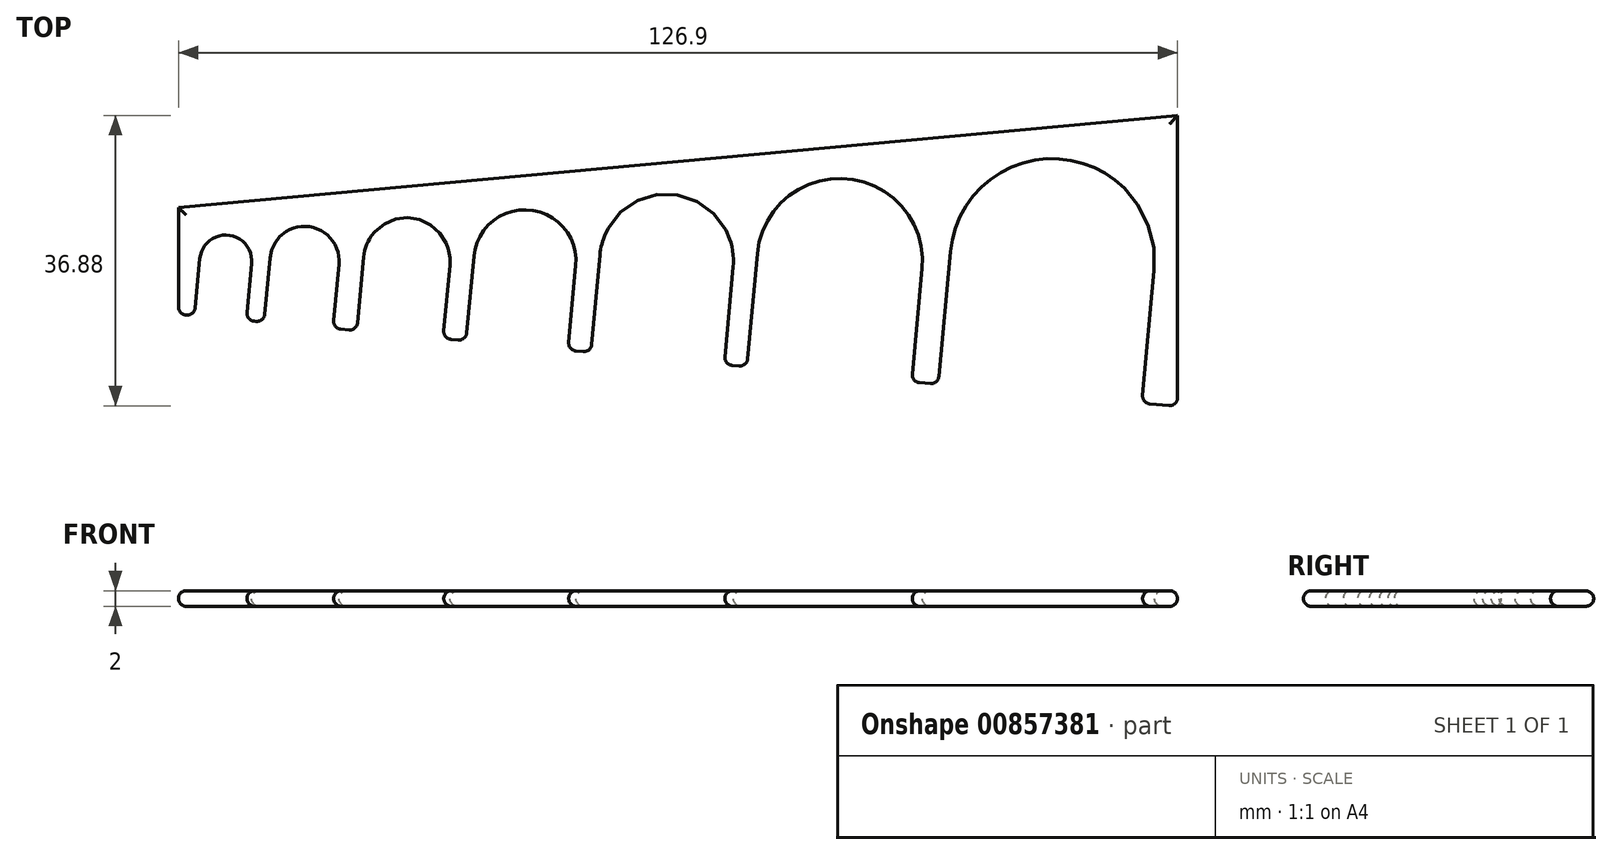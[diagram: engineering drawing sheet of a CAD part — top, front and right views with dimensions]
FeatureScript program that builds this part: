
annotation { "Feature Type Name" : "Feature", "Feature Type Description" : "" }
export const myFeature = defineFeature(function(context is Context, id is Id, definition is map)
    precondition{}
    {
        {
            var Q0;
            Q0=qCreatedBy(makeId("Top.planeOp"),FACE);
            var sketch = newSketch(context, id + "F0", { "sketchPlane" : qUnion([Q0])});
            skCircle(sketch, "E0", {"center": v(0, 0) * mm, "radius": 4.4 * mm});
            skCircle(sketch, "E1", {"center": v(-10, 0) * mm, "radius": 3.3 * mm});
            skCircle(sketch, "E2", {"center": v(13, 0) * mm, "radius": 5.5 * mm});
            skCircle(sketch, "E3", {"center": v(28, 0) * mm, "radius": 6.5 * mm});
            skArc(sketch, "E4", {"start": v(54.46, -0.78) * mm, "mid": v(46.78, 8.46) * mm, "end": v(37.54, 0.78) * mm});
            skArc(sketch, "E5", {"start": v(66.14, -10.33) * mm, "mid": v(67.03, -10.46) * mm, "end": v(67.94, -10.5) * mm});
            skCircle(sketch, "E6", {"center": v(95, 0) * mm, "radius": 13 * mm});
            skLineSegment(sketch, "E7", {"start": v(-16, -6.76) * mm, "end": v(-16, 0) * mm});
            skLineSegment(sketch, "E8", {"start": v(110.9, 0) * mm, "end": v(110.9, -18.49) * mm});
            skLineSegment(sketch, "E9", {"start": v(-10, -3.3) * mm, "end": v(95, -13) * mm});
            skLineSegment(sketch, "E10.0", {"start": v(-16, -6.76) * mm, "end": v(110.9, -18.49) * mm});
            skLineSegment(sketch, "E11", {"start": v(-16, 0) * mm, "end": v(110.9, 0) * mm});
            skLineSegment(sketch, "E12.MirrorCS", {"start": v(-16, 6.76) * mm, "end": v(110.9, 18.49) * mm});
            skLineSegment(sketch, "E13", {"start": v(-16, 0) * mm, "end": v(-16, 6.76) * mm});
            skLineSegment(sketch, "E14", {"start": v(110.9, 0) * mm, "end": v(110.9, 18.49) * mm});
            skLineSegment(sketch, "E15", {"start": v(-10, 0) * mm, "end": v(-10.67, -7.26) * mm});
            skLineSegment(sketch, "E16", {"start": v(0, 0) * mm, "end": v(-0.75, -8.17) * mm});
            skLineSegment(sketch, "E17", {"start": v(13, 0) * mm, "end": v(12.14, -9.36) * mm});
            skLineSegment(sketch, "E18", {"start": v(28, 0) * mm, "end": v(27, -10.74) * mm});
            skLineSegment(sketch, "E19", {"start": v(68, 0) * mm, "end": v(66.67, -14.4) * mm});
            skLineSegment(sketch, "E20", {"start": v(95, 0) * mm, "end": v(93.44, -16.87) * mm});
            skLineSegment(sketch, "E21", {"start": v(80.5, -15.68) * mm, "end": v(82.06, 1.2) * mm});
            skLineSegment(sketch, "E22", {"start": v(106.39, -18.07) * mm, "end": v(107.94, -1.2) * mm});
            skLineSegment(sketch, "E23", {"start": v(77.13, -15.37) * mm, "end": v(78.46, -0.97) * mm});
            skLineSegment(sketch, "E24", {"start": v(56.21, -13.43) * mm, "end": v(57.54, 0.97) * mm});
            skArc(sketch, "E25.trimOffspring", {"start": v(78.46, -0.97) * mm, "mid": v(68.97, 10.46) * mm, "end": v(57.54, 0.97) * mm});
            skLineSegment(sketch, "E26", {"start": v(54.46, -0.78) * mm, "end": v(53.32, -13.17) * mm});
            skLineSegment(sketch, "E27", {"start": v(37.54, 0.78) * mm, "end": v(36.4, -11.6) * mm});
            skLineSegment(sketch, "E28", {"start": v(28, 0) * mm, "end": v(34.47, -0.6) * mm});
            skLineSegment(sketch, "E29", {"start": v(34.47, -0.6) * mm, "end": v(33.48, -11.33) * mm});
            skLineSegment(sketch, "E30", {"start": v(28, 0) * mm, "end": v(21.53, 0.6) * mm});
            skLineSegment(sketch, "E31", {"start": v(21.53, 0.6) * mm, "end": v(20.54, -10.14) * mm});
            skLineSegment(sketch, "E32", {"start": v(13, 0) * mm, "end": v(18.48, -0.5) * mm});
            skLineSegment(sketch, "E33", {"start": v(18.48, -0.5) * mm, "end": v(17.61, -9.87) * mm});
            skLineSegment(sketch, "E34", {"start": v(13, 0) * mm, "end": v(7.52, 0.5) * mm});
            skLineSegment(sketch, "E35", {"start": v(7.52, 0.5) * mm, "end": v(6.66, -8.86) * mm});
            skLineSegment(sketch, "E36", {"start": v(0, 0) * mm, "end": v(4.38, -0.4) * mm});
            skLineSegment(sketch, "E37", {"start": v(4.38, -0.4) * mm, "end": v(3.63, -8.58) * mm});
            skLineSegment(sketch, "E38", {"start": v(0, 0) * mm, "end": v(-4.38, 0.4) * mm});
            skLineSegment(sketch, "E39", {"start": v(-4.38, 0.4) * mm, "end": v(-5.14, -7.77) * mm});
            skLineSegment(sketch, "E40", {"start": v(-10, 0) * mm, "end": v(-6.71, -0.3) * mm});
            skLineSegment(sketch, "E41", {"start": v(-6.71, -0.3) * mm, "end": v(-7.38, -7.56) * mm});
            skLineSegment(sketch, "E42", {"start": v(-10, 0) * mm, "end": v(-13.29, 0.3) * mm});
            skLineSegment(sketch, "E43", {"start": v(-13.29, 0.3) * mm, "end": v(-13.96, -6.95) * mm});
            skSolve(sketch);
        }
        {
            var Q0;
            Q0=makeQuery(id+"F0.imprint","IMPRINT",FACE,{"disambiguationData":[TD([[makeQuery(id+"F0.imprint","IMPRINT",EDGE,{"derivedFrom":sQuery(id+"F0.wireOp",EDGE,"E12.MirrorCS")}),-1.0]])]});
            var Q1;
            {var subQ0=sQuery(id+"F0.wireOp",EDGE,"E7");Q1=makeQuery(id+"F0.imprint","IMPRINT",FACE,{"disambiguationData":[TD([[makeQuery(id+"F0.imprint","IMPRINT",EDGE,{"derivedFrom":subQ0}),-1.0]])]});}
            var Q2;
            {var subQ1=sQuery(id+"F0.wireOp",EDGE,"E9");var subQ7=sQuery(id+"F0.wireOp",EDGE,"E41");var subQ8=makeQuery(id+"F0.imprint","INTERSECT",VERTEX,{"derivedFrom":[subQ1,subQ7]});Q2=makeQuery(id+"F0.imprint","IMPRINT",FACE,{"disambiguationData":[TD([[makeQuery(id+"F0.imprint","IMPRINT",EDGE,{"disambiguationData":[TD([[subQ8,-1.0]])],"derivedFrom":subQ1}),1.0]])]});}
            var Q3;
            {var subQ0=sQuery(id+"F0.wireOp",EDGE,"E41");var subQ1=sQuery(id+"F0.wireOp",EDGE,"E9");var subQ2=makeQuery(id+"F0.imprint","INTERSECT",VERTEX,{"derivedFrom":[subQ1,subQ0]});Q3=makeQuery(id+"F0.imprint","IMPRINT",FACE,{"disambiguationData":[TD([[makeQuery(id+"F0.imprint","IMPRINT",EDGE,{"disambiguationData":[TD([[subQ2,-1.0]])],"derivedFrom":subQ1}),-1.0]])]});}
            var Q4;
            {var subQ1=sQuery(id+"F0.wireOp",EDGE,"E9");var subQ7=sQuery(id+"F0.wireOp",EDGE,"E37");var subQ8=makeQuery(id+"F0.imprint","INTERSECT",VERTEX,{"derivedFrom":[subQ1,subQ7]});Q4=makeQuery(id+"F0.imprint","IMPRINT",FACE,{"disambiguationData":[TD([[makeQuery(id+"F0.imprint","IMPRINT",EDGE,{"disambiguationData":[TD([[subQ8,-1.0]])],"derivedFrom":subQ1}),1.0]])]});}
            var Q5;
            {var subQ0=sQuery(id+"F0.wireOp",EDGE,"E37");var subQ1=sQuery(id+"F0.wireOp",EDGE,"E9");var subQ2=makeQuery(id+"F0.imprint","INTERSECT",VERTEX,{"derivedFrom":[subQ1,subQ0]});Q5=makeQuery(id+"F0.imprint","IMPRINT",FACE,{"disambiguationData":[TD([[makeQuery(id+"F0.imprint","IMPRINT",EDGE,{"disambiguationData":[TD([[subQ2,-1.0]])],"derivedFrom":subQ1}),-1.0]])]});}
            var Q6;
            {var subQ1=sQuery(id+"F0.wireOp",EDGE,"E9");var subQ7=sQuery(id+"F0.wireOp",EDGE,"E33");var subQ9=makeQuery(id+"F0.imprint","INTERSECT",VERTEX,{"derivedFrom":[subQ1,subQ7]});Q6=makeQuery(id+"F0.imprint","IMPRINT",FACE,{"disambiguationData":[TD([[makeQuery(id+"F0.imprint","IMPRINT",EDGE,{"disambiguationData":[TD([[subQ9,-1.0]])],"derivedFrom":subQ1}),1.0]])]});}
            var Q7;
            {var subQ0=sQuery(id+"F0.wireOp",EDGE,"E33");var subQ1=sQuery(id+"F0.wireOp",EDGE,"E9");var subQ2=makeQuery(id+"F0.imprint","INTERSECT",VERTEX,{"derivedFrom":[subQ1,subQ0]});Q7=makeQuery(id+"F0.imprint","IMPRINT",FACE,{"disambiguationData":[TD([[makeQuery(id+"F0.imprint","IMPRINT",EDGE,{"disambiguationData":[TD([[subQ2,-1.0]])],"derivedFrom":subQ1}),-1.0]])]});}
            var Q8;
            {var subQ5=sQuery(id+"F0.wireOp",EDGE,"E9");var subQ7=sQuery(id+"F0.wireOp",EDGE,"E29");var subQ8=makeQuery(id+"F0.imprint","INTERSECT",VERTEX,{"derivedFrom":[subQ5,subQ7]});Q8=makeQuery(id+"F0.imprint","IMPRINT",FACE,{"disambiguationData":[TD([[makeQuery(id+"F0.imprint","IMPRINT",EDGE,{"disambiguationData":[TD([[subQ8,-1.0]])],"derivedFrom":subQ5}),1.0]])]});}
            var Q9;
            {var subQ0=sQuery(id+"F0.wireOp",EDGE,"E29");var subQ1=sQuery(id+"F0.wireOp",EDGE,"E9");var subQ2=makeQuery(id+"F0.imprint","INTERSECT",VERTEX,{"derivedFrom":[subQ1,subQ0]});Q9=makeQuery(id+"F0.imprint","IMPRINT",FACE,{"disambiguationData":[TD([[makeQuery(id+"F0.imprint","IMPRINT",EDGE,{"disambiguationData":[TD([[subQ2,-1.0]])],"derivedFrom":subQ1}),-1.0]])]});}
            var Q10;
            {var subQ5=sQuery(id+"F0.wireOp",EDGE,"E4");var subQ7=sQuery(id+"F0.wireOp",EDGE,"E26");var subQ8=makeQuery(id+"F0.imprint","INTERSECT",VERTEX,{"derivedFrom":[subQ5,subQ7]});Q10=makeQuery(id+"F0.imprint","IMPRINT",FACE,{"disambiguationData":[TD([[makeQuery(id+"F0.imprint","IMPRINT",EDGE,{"disambiguationData":[TD([[subQ8,-1.0]])],"derivedFrom":subQ5}),-1.0]])]});}
            var Q11;
            {var subQ0=sQuery(id+"F0.wireOp",EDGE,"E26");var subQ1=sQuery(id+"F0.wireOp",EDGE,"E9");var subQ2=makeQuery(id+"F0.imprint","INTERSECT",VERTEX,{"derivedFrom":[subQ1,subQ0]});Q11=makeQuery(id+"F0.imprint","IMPRINT",FACE,{"disambiguationData":[TD([[makeQuery(id+"F0.imprint","IMPRINT",EDGE,{"disambiguationData":[TD([[subQ2,-1.0]])],"derivedFrom":subQ1}),-1.0]])]});}
            var Q12;
            {var subQ1=sQuery(id+"F0.wireOp",EDGE,"E9");var subQ6=sQuery(id+"F0.wireOp",EDGE,"E23");var subQ8=makeQuery(id+"F0.imprint","INTERSECT",VERTEX,{"derivedFrom":[subQ1,subQ6]});Q12=makeQuery(id+"F0.imprint","IMPRINT",FACE,{"disambiguationData":[TD([[makeQuery(id+"F0.imprint","IMPRINT",EDGE,{"disambiguationData":[TD([[subQ8,-1.0]])],"derivedFrom":subQ1}),1.0]])]});}
            var Q13;
            {var subQ0=sQuery(id+"F0.wireOp",EDGE,"E23");var subQ1=sQuery(id+"F0.wireOp",EDGE,"E9");var subQ2=makeQuery(id+"F0.imprint","INTERSECT",VERTEX,{"derivedFrom":[subQ1,subQ0]});Q13=makeQuery(id+"F0.imprint","IMPRINT",FACE,{"disambiguationData":[TD([[makeQuery(id+"F0.imprint","IMPRINT",EDGE,{"disambiguationData":[TD([[subQ2,-1.0]])],"derivedFrom":subQ1}),-1.0]])]});}
            var Q14;
            {var subQ1=sQuery(id+"F0.wireOp",EDGE,"E8");Q14=makeQuery(id+"F0.imprint","IMPRINT",FACE,{"disambiguationData":[TD([[makeQuery(id+"F0.imprint","IMPRINT",EDGE,{"derivedFrom":subQ1}),-1.0]])]});}
            extrude(context, id + "F1", {"entities" : qUnion([Q0, Q1, Q2, Q3, Q4, Q5, Q6, Q7, Q8, Q9, Q10, Q11, Q12, Q13, Q14]), "depth" : 2 * mm, "offsetDistance" : 25 * mm});
        }
        {
            var Q0;
            Q0=makeQuery(id+"F1.opExtrude","CAP_FACE",FACE,{"disambiguationData":[OSD([sQuery(id+"F0.wireOp",EDGE,"E0"),sQuery(id+"F0.wireOp",EDGE,"E1"),sQuery(id+"F0.wireOp",EDGE,"E2"),sQuery(id+"F0.wireOp",EDGE,"E3"),sQuery(id+"F0.wireOp",EDGE,"E4"),sQuery(id+"F0.wireOp",EDGE,"E6"),sQuery(id+"F0.wireOp",EDGE,"E7"),sQuery(id+"F0.wireOp",EDGE,"E8"),sQuery(id+"F0.wireOp",EDGE,"E10.0"),sQuery(id+"F0.wireOp",EDGE,"E12.MirrorCS"),sQuery(id+"F0.wireOp",EDGE,"E13"),sQuery(id+"F0.wireOp",EDGE,"E14"),sQuery(id+"F0.wireOp",EDGE,"E21"),sQuery(id+"F0.wireOp",EDGE,"E22"),sQuery(id+"F0.wireOp",EDGE,"E23"),sQuery(id+"F0.wireOp",EDGE,"E24"),sQuery(id+"F0.wireOp",EDGE,"E25.trimOffspring"),sQuery(id+"F0.wireOp",EDGE,"E26"),sQuery(id+"F0.wireOp",EDGE,"E27"),sQuery(id+"F0.wireOp",EDGE,"E29"),sQuery(id+"F0.wireOp",EDGE,"E31"),sQuery(id+"F0.wireOp",EDGE,"E33"),sQuery(id+"F0.wireOp",EDGE,"E35"),sQuery(id+"F0.wireOp",EDGE,"E37"),sQuery(id+"F0.wireOp",EDGE,"E39"),sQuery(id+"F0.wireOp",EDGE,"E41"),sQuery(id+"F0.wireOp",EDGE,"E43")])],"isStart":false});
            var Q1;
            Q1=makeQuery(id+"F1.opExtrude","CAP_FACE",FACE,{"disambiguationData":[OSD([sQuery(id+"F0.wireOp",EDGE,"E0"),sQuery(id+"F0.wireOp",EDGE,"E1"),sQuery(id+"F0.wireOp",EDGE,"E2"),sQuery(id+"F0.wireOp",EDGE,"E3"),sQuery(id+"F0.wireOp",EDGE,"E4"),sQuery(id+"F0.wireOp",EDGE,"E6"),sQuery(id+"F0.wireOp",EDGE,"E7"),sQuery(id+"F0.wireOp",EDGE,"E8"),sQuery(id+"F0.wireOp",EDGE,"E10.0"),sQuery(id+"F0.wireOp",EDGE,"E12.MirrorCS"),sQuery(id+"F0.wireOp",EDGE,"E13"),sQuery(id+"F0.wireOp",EDGE,"E14"),sQuery(id+"F0.wireOp",EDGE,"E21"),sQuery(id+"F0.wireOp",EDGE,"E22"),sQuery(id+"F0.wireOp",EDGE,"E23"),sQuery(id+"F0.wireOp",EDGE,"E24"),sQuery(id+"F0.wireOp",EDGE,"E25.trimOffspring"),sQuery(id+"F0.wireOp",EDGE,"E26"),sQuery(id+"F0.wireOp",EDGE,"E27"),sQuery(id+"F0.wireOp",EDGE,"E29"),sQuery(id+"F0.wireOp",EDGE,"E31"),sQuery(id+"F0.wireOp",EDGE,"E33"),sQuery(id+"F0.wireOp",EDGE,"E35"),sQuery(id+"F0.wireOp",EDGE,"E37"),sQuery(id+"F0.wireOp",EDGE,"E39"),sQuery(id+"F0.wireOp",EDGE,"E41"),sQuery(id+"F0.wireOp",EDGE,"E43")])],"isStart":true});
            var Q2;
            Q2=makeQuery(id+"F1.opExtrude","SWEPT_EDGE",EDGE,{"disambiguationData":[OSD([sQuery(id+"F0.wireOp",EDGE,"E10.0"),sQuery(id+"F0.wireOp",EDGE,"E43")])]});
            var Q3;
            Q3=makeQuery(id+"F1.opExtrude","SWEPT_EDGE",EDGE,{"disambiguationData":[OSD([sQuery(id+"F0.wireOp",EDGE,"E7"),sQuery(id+"F0.wireOp",EDGE,"E10.0")])]});
            var Q4;
            Q4=makeQuery(id+"F1.opExtrude","SWEPT_EDGE",EDGE,{"disambiguationData":[OSD([sQuery(id+"F0.wireOp",EDGE,"E10.0"),sQuery(id+"F0.wireOp",EDGE,"E41")])]});
            var Q5;
            Q5=makeQuery(id+"F1.opExtrude","SWEPT_EDGE",EDGE,{"disambiguationData":[OSD([sQuery(id+"F0.wireOp",EDGE,"E10.0"),sQuery(id+"F0.wireOp",EDGE,"E39")])]});
            var Q6;
            Q6=makeQuery(id+"F1.opExtrude","SWEPT_EDGE",EDGE,{"disambiguationData":[OSD([sQuery(id+"F0.wireOp",EDGE,"E10.0"),sQuery(id+"F0.wireOp",EDGE,"E37")])]});
            var Q7;
            Q7=makeQuery(id+"F1.opExtrude","SWEPT_EDGE",EDGE,{"disambiguationData":[OSD([sQuery(id+"F0.wireOp",EDGE,"E10.0"),sQuery(id+"F0.wireOp",EDGE,"E35")])]});
            var Q8;
            Q8=makeQuery(id+"F1.opExtrude","SWEPT_EDGE",EDGE,{"disambiguationData":[OSD([sQuery(id+"F0.wireOp",EDGE,"E10.0"),sQuery(id+"F0.wireOp",EDGE,"E31")])]});
            var Q9;
            Q9=makeQuery(id+"F1.opExtrude","SWEPT_EDGE",EDGE,{"disambiguationData":[OSD([sQuery(id+"F0.wireOp",EDGE,"E10.0"),sQuery(id+"F0.wireOp",EDGE,"E33")])]});
            var Q10;
            Q10=makeQuery(id+"F1.opExtrude","SWEPT_EDGE",EDGE,{"disambiguationData":[OSD([sQuery(id+"F0.wireOp",EDGE,"E10.0"),sQuery(id+"F0.wireOp",EDGE,"E29")])]});
            var Q11;
            Q11=makeQuery(id+"F1.opExtrude","SWEPT_EDGE",EDGE,{"disambiguationData":[OSD([sQuery(id+"F0.wireOp",EDGE,"E10.0"),sQuery(id+"F0.wireOp",EDGE,"E27")])]});
            var Q12;
            Q12=makeQuery(id+"F1.opExtrude","SWEPT_EDGE",EDGE,{"disambiguationData":[OSD([sQuery(id+"F0.wireOp",EDGE,"E10.0"),sQuery(id+"F0.wireOp",EDGE,"E26")])]});
            var Q13;
            Q13=makeQuery(id+"F1.opExtrude","SWEPT_EDGE",EDGE,{"disambiguationData":[OSD([sQuery(id+"F0.wireOp",EDGE,"E10.0"),sQuery(id+"F0.wireOp",EDGE,"E24")])]});
            var Q14;
            Q14=makeQuery(id+"F1.opExtrude","SWEPT_EDGE",EDGE,{"disambiguationData":[OSD([sQuery(id+"F0.wireOp",EDGE,"E10.0"),sQuery(id+"F0.wireOp",EDGE,"E21")])]});
            var Q15;
            Q15=makeQuery(id+"F1.opExtrude","SWEPT_EDGE",EDGE,{"disambiguationData":[OSD([sQuery(id+"F0.wireOp",EDGE,"E10.0"),sQuery(id+"F0.wireOp",EDGE,"E23")])]});
            var Q16;
            Q16=makeQuery(id+"F1.opExtrude","SWEPT_EDGE",EDGE,{"disambiguationData":[OSD([sQuery(id+"F0.wireOp",EDGE,"E8"),sQuery(id+"F0.wireOp",EDGE,"E10.0")])]});
            var Q17;
            Q17=makeQuery(id+"F1.opExtrude","SWEPT_EDGE",EDGE,{"disambiguationData":[OSD([sQuery(id+"F0.wireOp",EDGE,"E10.0"),sQuery(id+"F0.wireOp",EDGE,"E22")])]});
            fillet(context, id + "F2", {"entities" : qUnion([Q0, Q1, Q2, Q3, Q4, Q5, Q6, Q7, Q8, Q9, Q10, Q11, Q12, Q13, Q14, Q15, Q16, Q17]), "radius" : 1 * mm, "tangentPropagation" : true, "allowEdgeOverflow" : false});
        }
    });
